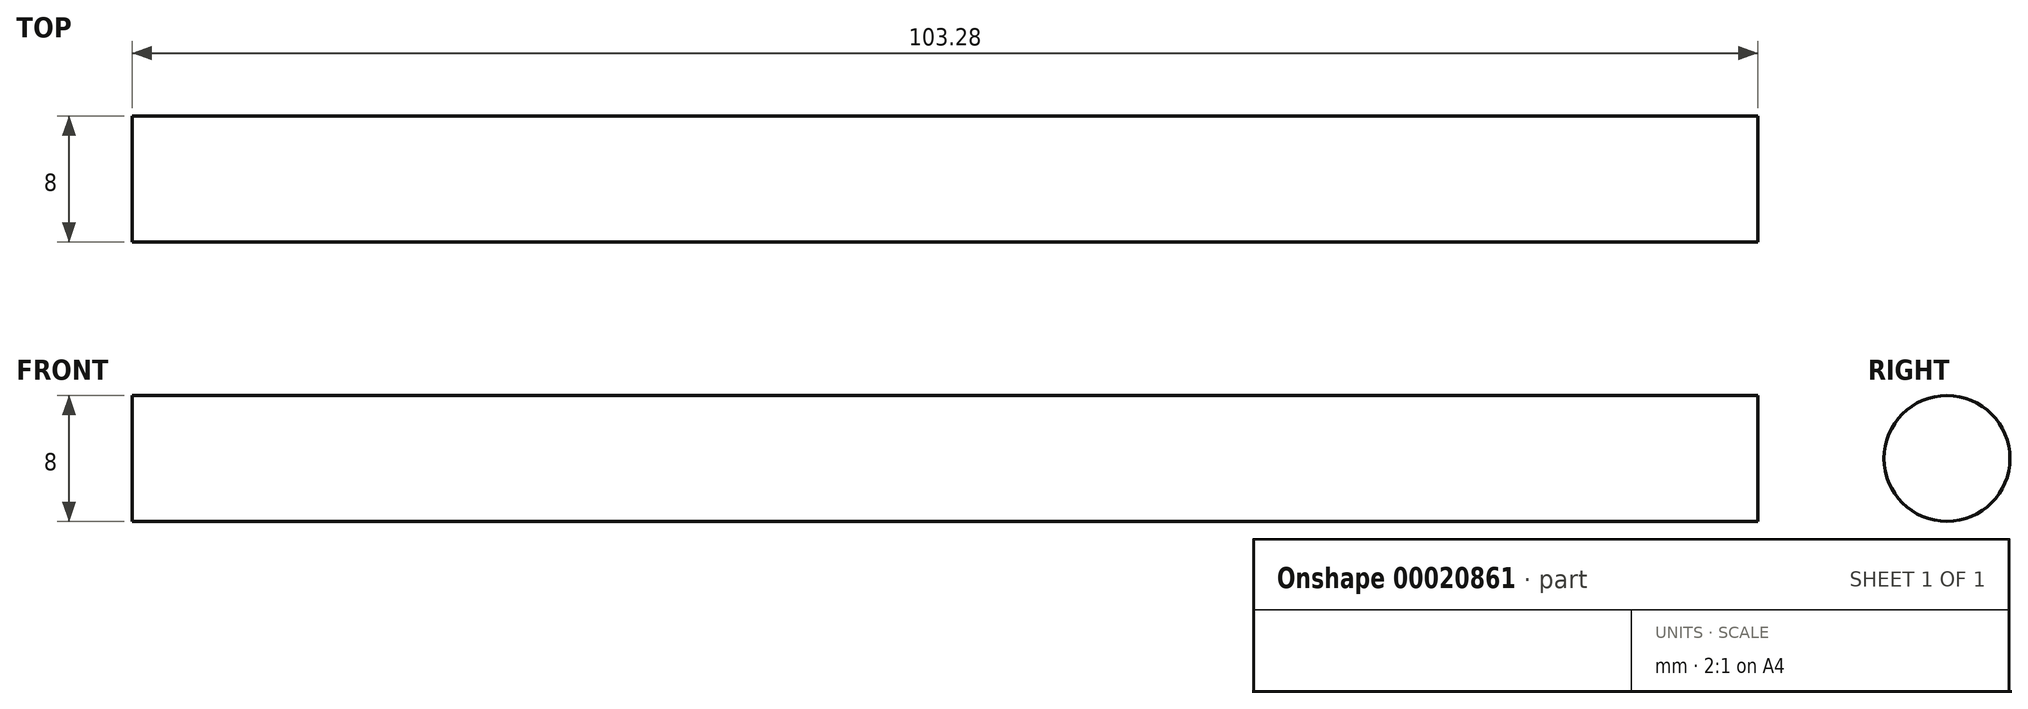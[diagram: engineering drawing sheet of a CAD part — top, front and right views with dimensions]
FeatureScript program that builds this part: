
annotation { "Feature Type Name" : "Feature", "Feature Type Description" : "" }
export const myFeature = defineFeature(function(context is Context, id is Id, definition is map)
    precondition{}
    {
        {
            var Q0;
            Q0=qCreatedBy(makeId("Right.planeOp"),FACE);
            var sketch = newSketch(context, id + "F0", { "sketchPlane" : qUnion([Q0])});
            skCircle(sketch, "E0", {"center": v(0, 0) * mm, "radius": 4 * mm});
            skSolve(sketch);
        }
        {
            var Q0;
            Q0=makeQuery(id+"F0.imprint","IMPRINT",FACE,{"disambiguationData":[TD([[makeQuery(id+"F0.imprint","IMPRINT",EDGE,{"derivedFrom":sQuery(id+"F0.wireOp",EDGE,"E0")}),1.0]])]});
            extrude(context, id + "F1", {"entities" : qUnion([Q0]), "endBound" : BoundingType.SYMMETRIC, "depth" : 103.28 * mm});
        }
    });
